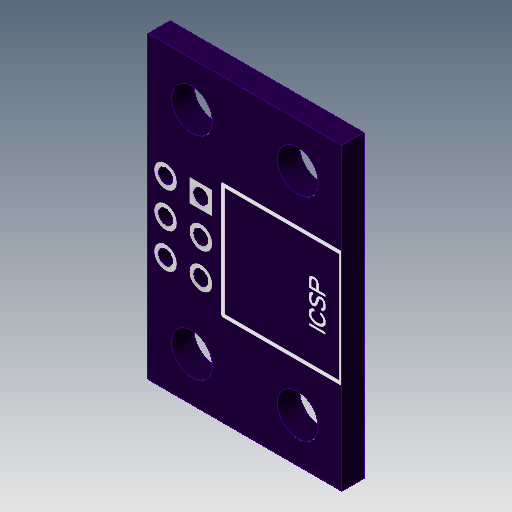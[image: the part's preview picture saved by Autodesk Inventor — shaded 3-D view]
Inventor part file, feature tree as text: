
AUTODESK INVENTOR PART (.ipt)
format: ipt  version: 2018 (Build 220112000, 112)  size: 180,736 bytes
history: native  units: mm
features: other x4, sketch x2
ambient origin geometry x8: Origin, YZ Plane, XZ Plane, XY Plane, X Axis, Y Axis, Z Axis, Center Point
bodies: Solid1 (feature_tree)
feature tree (6):
  other  "Decal1"
  other  "Decal2"
  sketch  "Sketch1"
  other  "Image1"
  sketch  "Sketch2"
  other  "Image2"
